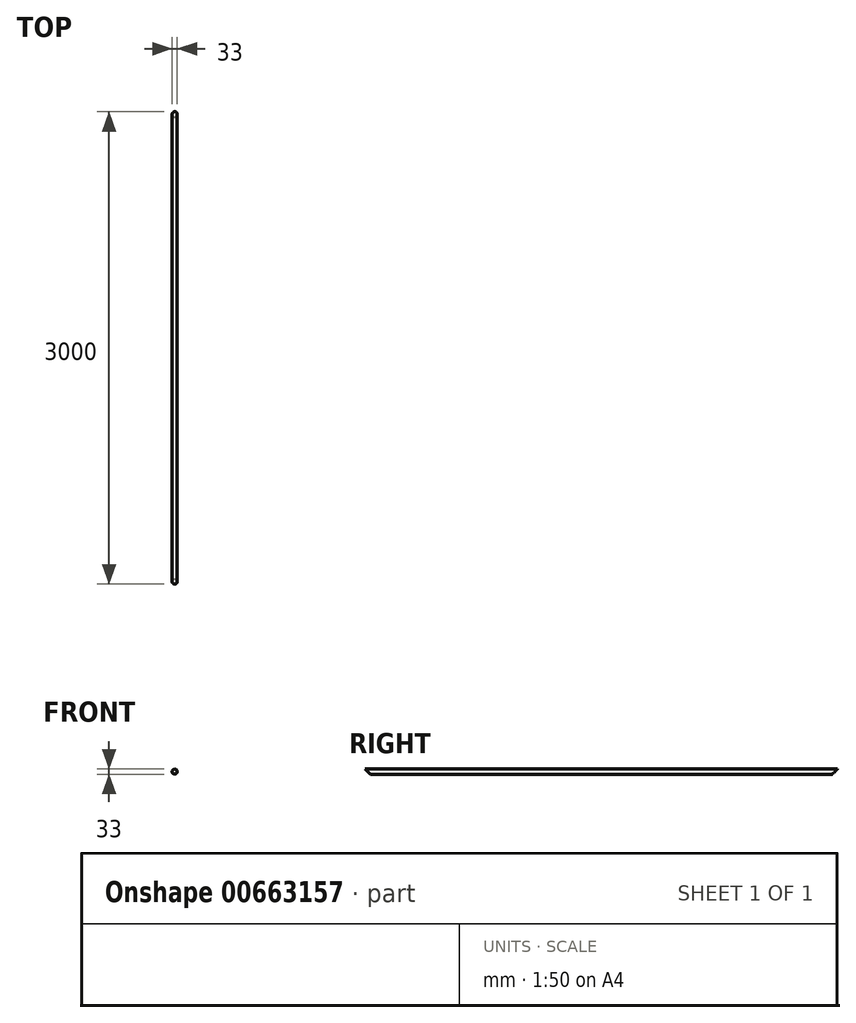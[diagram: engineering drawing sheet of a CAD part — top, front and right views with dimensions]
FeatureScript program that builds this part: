
annotation { "Feature Type Name" : "Feature", "Feature Type Description" : "" }
export const myFeature = defineFeature(function(context is Context, id is Id, definition is map)
    precondition{}
    {
        {
            var Q0;
            Q0=qCreatedBy(makeId("Front.planeOp"),FACE);
            var sketch = newSketch(context, id + "F0", { "sketchPlane" : qUnion([Q0])});
            skLineSegment(sketch, "E0.bottom", {"start": v(16.5, 16.5) * mm, "end": v(-16.5, 16.5) * mm});
            skLineSegment(sketch, "E0.top", {"start": v(16.5, -16.5) * mm, "end": v(-16.5, -16.5) * mm});
            skLineSegment(sketch, "E0.left", {"start": v(16.5, 16.5) * mm, "end": v(16.5, -16.5) * mm});
            skLineSegment(sketch, "E0.right", {"start": v(-16.5, 16.5) * mm, "end": v(-16.5, -16.5) * mm});
            skPoint(sketch, "E0.middle", {"position": v(0, 0) * mm});
            skSolve(sketch);
        }
        {
            var Q0;
            Q0=makeQuery(id+"F0.imprint","IMPRINT",FACE,{"disambiguationData":[TD([[makeQuery(id+"F0.imprint","IMPRINT",EDGE,{"derivedFrom":sQuery(id+"F0.wireOp",EDGE,"E0.bottom")}),1.0]])]});
            extrude(context, id + "F1", {"entities" : qUnion([Q0]), "endBound" : BoundingType.SYMMETRIC, "depth" : 3000 * mm, "offsetDistance" : 25 * mm});
        }
        {
            var Q0;
            Q0=makeQuery(id+"F1.opExtrude","SWEPT_FACE",FACE,{"disambiguationData":[OSD([sQuery(id+"F0.wireOp",EDGE,"E0.left")])]});
            var sketch = newSketch(context, id + "F2", { "sketchPlane" : qUnion([Q0])});
            skLineSegment(sketch, "E1", {"start": v(-1500, 16.5) * mm, "end": v(-1467, -16.5) * mm});
            skLineSegment(sketch, "E2", {"start": v(1500, 16.5) * mm, "end": v(1467, -16.5) * mm});
            skSolve(sketch);
        }
        {
            var Q0;
            {var subQ0=sQuery(id+"F2.wireOp",EDGE,"E2");Q0=makeQuery(id+"F2.imprint","IMPRINT",FACE,{"disambiguationData":[TD([[makeQuery(id+"F2.imprint","IMPRINT",EDGE,{"derivedFrom":subQ0}),1.0]])]});}
            var Q1;
            {var subQ0=sQuery(id+"F2.wireOp",EDGE,"E1");Q1=makeQuery(id+"F2.imprint","IMPRINT",FACE,{"disambiguationData":[TD([[makeQuery(id+"F2.imprint","IMPRINT",EDGE,{"derivedFrom":subQ0}),-1.0]])]});}
            extrude(context, id + "F3", {"entities" : qUnion([Q0, Q1]), "operationType" : NewBodyOperationType.REMOVE, "oppositeDirection" : true, "depth" : 50 * mm, "offsetDistance" : 25 * mm});
        }
        {
            var Q0;
            Q0=makeQuery(id+"F1.opExtrude","SWEPT_EDGE",EDGE,{"disambiguationData":[OSD([sQuery(id+"F0.wireOp",EDGE,"E0.bottom"),sQuery(id+"F0.wireOp",EDGE,"E0.left")])]});
            var Q1;
            Q1=makeQuery(id+"F1.opExtrude","SWEPT_EDGE",EDGE,{"disambiguationData":[OSD([sQuery(id+"F0.wireOp",EDGE,"E0.top"),sQuery(id+"F0.wireOp",EDGE,"E0.left")])]});
            var Q2;
            Q2=makeQuery(id+"F1.opExtrude","SWEPT_EDGE",EDGE,{"disambiguationData":[OSD([sQuery(id+"F0.wireOp",EDGE,"E0.top"),sQuery(id+"F0.wireOp",EDGE,"E0.right")])]});
            var Q3;
            Q3=makeQuery(id+"F1.opExtrude","SWEPT_EDGE",EDGE,{"disambiguationData":[OSD([sQuery(id+"F0.wireOp",EDGE,"E0.bottom"),sQuery(id+"F0.wireOp",EDGE,"E0.right")])]});
            fillet(context, id + "F4", {"entities" : qUnion([Q0, Q1, Q2, Q3]), "radius" : (33 / 2) * mm, "tangentPropagation" : true, "allowEdgeOverflow" : false});
        }
    });
